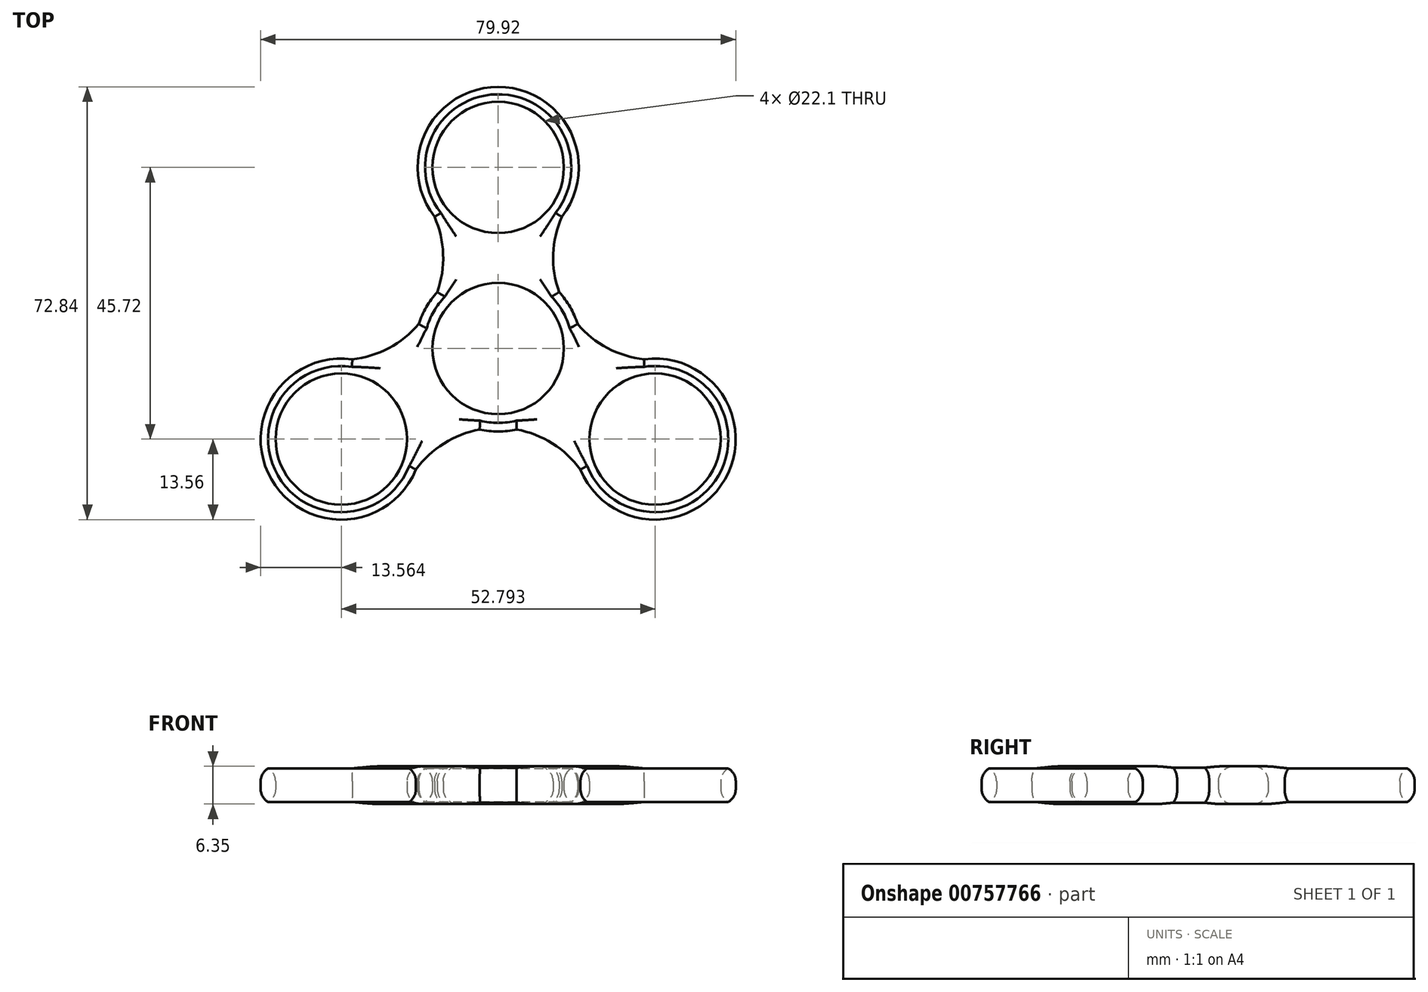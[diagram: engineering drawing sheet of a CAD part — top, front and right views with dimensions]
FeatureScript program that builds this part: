
annotation { "Feature Type Name" : "Feature", "Feature Type Description" : "" }
export const myFeature = defineFeature(function(context is Context, id is Id, definition is map)
    precondition{}
    {
        {
            var Q0;
            Q0=qCreatedBy(makeId("Top.planeOp"),FACE);
            var sketch = newSketch(context, id + "F0", { "sketchPlane" : qUnion([Q0])});
            skCircle(sketch, "E0", {"center": v(0, 0) * mm, "radius": 13.97 * mm});
            skCircle(sketch, "E1", {"center": v(0, 0) * mm, "radius": 11.05 * mm});
            skLineSegment(sketch, "E2", {"start": v(0, 0) * mm, "end": v(0, 30.48) * mm});
            skCircle(sketch, "E3", {"center": v(0, 30.48) * mm, "radius": 11.05 * mm});
            skCircle(sketch, "E4", {"center": v(0, 30.48) * mm, "radius": 13.56 * mm});
            skCircle(sketch, "E5.1.0", {"center": v(-26.4, -15.24) * mm, "radius": 11.05 * mm});
            skCircle(sketch, "E5.1.1", {"center": v(-26.4, -15.24) * mm, "radius": 13.56 * mm});
            skCircle(sketch, "E5.2.0", {"center": v(26.4, -15.24) * mm, "radius": 11.05 * mm});
            skCircle(sketch, "E5.2.1", {"center": v(26.4, -15.24) * mm, "radius": 13.56 * mm});
            skLineSegment(sketch, "E6", {"start": v(0, 0) * mm, "end": v(-26.4, 15.24) * mm});
            skArc(sketch, "E7", {"start": v(-28.24, -1.8) * mm, "mid": v(-11.55, 6.67) * mm, "end": v(-12.55, 25.36) * mm});
            skArc(sketch, "E8.1.0", {"start": v(15.68, -23.55) * mm, "mid": v(0, -13.33) * mm, "end": v(-15.68, -23.55) * mm});
            skArc(sketch, "E8.2.0", {"start": v(12.55, 25.36) * mm, "mid": v(11.55, 6.67) * mm, "end": v(28.24, -1.8) * mm});
            skSolve(sketch);
        }
        {
            var Q0;
            Q0=qSketchRegion(id+"F0",true);
            extrude(context, id + "F1", {"entities" : qUnion([Q0]), "depth" : 6.35 * mm, "offsetDistance" : 25.4 * mm});
        }
        {
            var Q0;
            Q0=makeQuery(id+"F1.opExtrude","CAP_FACE",FACE,{"disambiguationData":[OSD([sQuery(id+"F0.wireOp",EDGE,"E0"),sQuery(id+"F0.wireOp",EDGE,"E1"),sQuery(id+"F0.wireOp",EDGE,"E3"),sQuery(id+"F0.wireOp",EDGE,"E4"),sQuery(id+"F0.wireOp",EDGE,"E5.1.0"),sQuery(id+"F0.wireOp",EDGE,"E5.1.1"),sQuery(id+"F0.wireOp",EDGE,"E5.2.0"),sQuery(id+"F0.wireOp",EDGE,"E5.2.1"),sQuery(id+"F0.wireOp",EDGE,"E7"),sQuery(id+"F0.wireOp",EDGE,"E8.1.0"),sQuery(id+"F0.wireOp",EDGE,"E8.2.0")])],"isStart":false});
            var Q1;
            Q1=makeQuery(id+"F1.opExtrude","CAP_FACE",FACE,{"disambiguationData":[OSD([sQuery(id+"F0.wireOp",EDGE,"E0"),sQuery(id+"F0.wireOp",EDGE,"E1"),sQuery(id+"F0.wireOp",EDGE,"E3"),sQuery(id+"F0.wireOp",EDGE,"E4"),sQuery(id+"F0.wireOp",EDGE,"E5.1.0"),sQuery(id+"F0.wireOp",EDGE,"E5.1.1"),sQuery(id+"F0.wireOp",EDGE,"E5.2.0"),sQuery(id+"F0.wireOp",EDGE,"E5.2.1"),sQuery(id+"F0.wireOp",EDGE,"E7"),sQuery(id+"F0.wireOp",EDGE,"E8.1.0"),sQuery(id+"F0.wireOp",EDGE,"E8.2.0")])],"isStart":true});
            fillet(context, id + "F2", {"entities" : qUnion([Q0, Q1]), "radius" : 2.54 * mm, "tangentPropagation" : true, "allowEdgeOverflow" : false});
        }
    });
